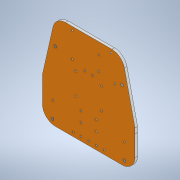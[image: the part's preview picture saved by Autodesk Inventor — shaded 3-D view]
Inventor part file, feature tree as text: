
AUTODESK INVENTOR PART (.ipt)
format: ipt  version: 2020 (Build 240168000, 168)  size: 229,376 bytes
history: native  units: in
note: dims shown in document units (in); Inventor stores cm internally (conversion verified against a paired STEP export)
features: imported_body x1, extrude x1, fillet x1
ambient origin geometry x8: Origin, YZ Plane, XZ Plane, XY Plane, X Axis, Y Axis, Z Axis, Center Point
bodies: Solid1 (feature_tree)
feature tree (3):
  imported_body  "Base"
  extrude  "Extrusion1"  Depth=0.1969in TaperAngle=0.0deg
  fillet  "Fillet1"  Radius=0.9843in
